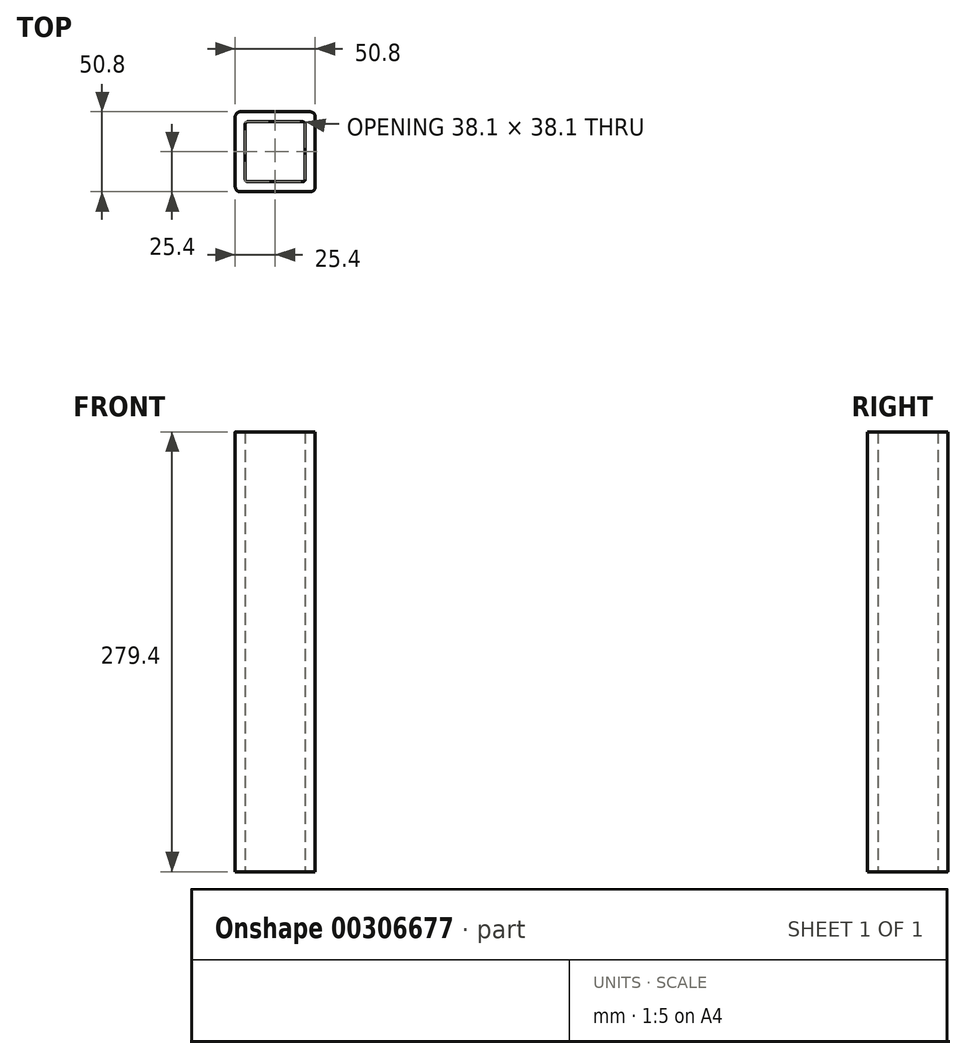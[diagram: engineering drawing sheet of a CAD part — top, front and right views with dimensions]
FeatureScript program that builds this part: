
annotation { "Feature Type Name" : "Feature", "Feature Type Description" : "" }
export const myFeature = defineFeature(function(context is Context, id is Id, definition is map)
    precondition{}
    {
        {
            var Q0;
            Q0=qCreatedBy(makeId("Top.planeOp"),FACE);
            var sketch = newSketch(context, id + "F0", { "sketchPlane" : qUnion([Q0])});
            skLineSegment(sketch, "E0.bottom", {"start": v(-22.22, 25.4) * mm, "end": v(22.23, 25.4) * mm});
            skLineSegment(sketch, "E0.top", {"start": v(-22.23, -25.4) * mm, "end": v(22.23, -25.4) * mm});
            skLineSegment(sketch, "E0.left", {"start": v(-25.4, 22.22) * mm, "end": v(-25.4, -22.23) * mm});
            skLineSegment(sketch, "E0.right", {"start": v(25.4, 22.22) * mm, "end": v(25.4, -22.23) * mm});
            skPoint(sketch, "E0.middle", {"position": v(0, 0) * mm});
            skPoint(sketch, "E1.visualSharp", {"position": v(-25.4, 25.4) * mm});
            skArc(sketch, "E1.filletArc", {"start": v(-22.22, 25.4) * mm, "mid": v(-24.47, 24.47) * mm, "end": v(-25.4, 22.22) * mm});
            skPoint(sketch, "E2.visualSharp", {"position": v(-25.4, -25.4) * mm});
            skArc(sketch, "E2.filletArc", {"start": v(-25.4, -22.23) * mm, "mid": v(-24.47, -24.47) * mm, "end": v(-22.23, -25.4) * mm});
            skPoint(sketch, "E3.visualSharp", {"position": v(25.4, -25.4) * mm});
            skArc(sketch, "E3.filletArc", {"start": v(22.23, -25.4) * mm, "mid": v(24.47, -24.47) * mm, "end": v(25.4, -22.23) * mm});
            skPoint(sketch, "E4.visualSharp", {"position": v(25.4, 25.4) * mm});
            skArc(sketch, "E4.filletArc", {"start": v(25.4, 22.22) * mm, "mid": v(24.47, 24.47) * mm, "end": v(22.23, 25.4) * mm});
            skLineSegment(sketch, "E5.0", {"start": v(-17.46, 19.05) * mm, "end": v(17.46, 19.05) * mm});
            skLineSegment(sketch, "E5.1", {"start": v(-19.05, 17.46) * mm, "end": v(-19.05, -17.46) * mm});
            skLineSegment(sketch, "E5.2", {"start": v(-17.46, -19.05) * mm, "end": v(17.46, -19.05) * mm});
            skLineSegment(sketch, "E5.3", {"start": v(19.05, 17.46) * mm, "end": v(19.05, -17.46) * mm});
            skPoint(sketch, "E6.visualSharp", {"position": v(-19.05, 19.05) * mm});
            skArc(sketch, "E6.filletArc", {"start": v(-17.46, 19.05) * mm, "mid": v(-18.59, 18.59) * mm, "end": v(-19.05, 17.46) * mm});
            skPoint(sketch, "E7.visualSharp", {"position": v(-19.05, -19.05) * mm});
            skArc(sketch, "E7.filletArc", {"start": v(-19.05, -17.46) * mm, "mid": v(-18.59, -18.59) * mm, "end": v(-17.46, -19.05) * mm});
            skPoint(sketch, "E8.visualSharp", {"position": v(19.05, -19.05) * mm});
            skArc(sketch, "E8.filletArc", {"start": v(17.46, -19.05) * mm, "mid": v(18.59, -18.59) * mm, "end": v(19.05, -17.46) * mm});
            skPoint(sketch, "E9.visualSharp", {"position": v(19.05, 19.05) * mm});
            skArc(sketch, "E9.filletArc", {"start": v(19.05, 17.46) * mm, "mid": v(18.59, 18.59) * mm, "end": v(17.46, 19.05) * mm});
            skSolve(sketch);
        }
        {
            var Q0;
            Q0=makeQuery(id+"F0.imprint","IMPRINT",FACE,{"disambiguationData":[TD([[makeQuery(id+"F0.imprint","IMPRINT",EDGE,{"derivedFrom":sQuery(id+"F0.wireOp",EDGE,"E0.bottom")}),-1.0]])]});
            extrude(context, id + "F1", {"entities" : qUnion([Q0]), "depth" : 279.4 * mm});
        }
    });
